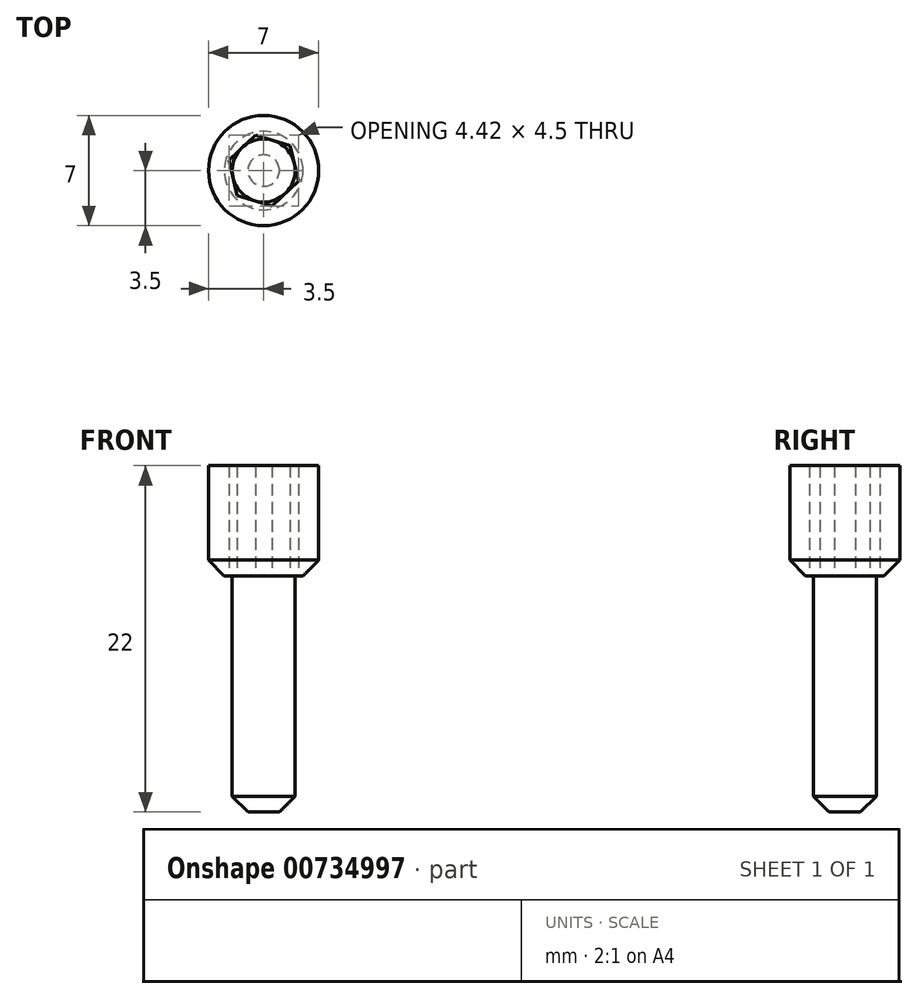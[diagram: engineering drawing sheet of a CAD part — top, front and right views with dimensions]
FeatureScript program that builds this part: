
annotation { "Feature Type Name" : "Feature", "Feature Type Description" : "" }
export const myFeature = defineFeature(function(context is Context, id is Id, definition is map)
    precondition{}
    {
        {
            var Q0;
            Q0=qCreatedBy(makeId("Top.planeOp"),FACE);
            var sketch = newSketch(context, id + "F0", { "sketchPlane" : qUnion([Q0])});
            skCircle(sketch, "E0", {"center": v(0, 0) * mm, "radius": 3.5 * mm});
            skCircle(sketch, "E1.cCircle", {"center": v(0, 0) * mm, "radius": 2 * mm, "construction": true});
            skLineSegment(sketch, "E1.0", {"start": v(2.21, -0.67) * mm, "end": v(0.53, -2.25) * mm});
            skLineSegment(sketch, "E1.1", {"start": v(0.53, -2.25) * mm, "end": v(-1.68, -1.58) * mm});
            skLineSegment(sketch, "E1.2", {"start": v(-1.68, -1.58) * mm, "end": v(-2.21, 0.67) * mm});
            skLineSegment(sketch, "E1.3", {"start": v(-2.21, 0.67) * mm, "end": v(-0.53, 2.25) * mm});
            skLineSegment(sketch, "E1.4", {"start": v(-0.53, 2.25) * mm, "end": v(1.68, 1.58) * mm});
            skLineSegment(sketch, "E1.5", {"start": v(1.68, 1.58) * mm, "end": v(2.21, -0.67) * mm});
            skPoint(sketch, "E1.0.midPoint", {"position": v(1.37, -1.46) * mm});
            skSolve(sketch);
        }
        {
            var Q0;
            Q0=makeQuery(id+"F0.imprint","IMPRINT",FACE,{"disambiguationData":[TD([[makeQuery(id+"F0.imprint","IMPRINT",EDGE,{"derivedFrom":sQuery(id+"F0.wireOp",EDGE,"E0")}),1.0]])]});
            extrude(context, id + "F1", {"entities" : qUnion([Q0]), "depth" : 7 * mm, "offsetDistance" : 25 * mm});
        }
        {
            var Q0;
            Q0=qCreatedBy(makeId("Top.planeOp"),FACE);
            var sketch = newSketch(context, id + "F2", { "sketchPlane" : qUnion([Q0])});
            skCircle(sketch, "E2.cCircle", {"center": v(0, 0) * mm, "radius": 2 * mm, "construction": true});
            skLineSegment(sketch, "E2.0", {"start": v(1.68, 1.58) * mm, "end": v(2.21, -0.67) * mm});
            skLineSegment(sketch, "E2.1", {"start": v(2.21, -0.67) * mm, "end": v(0.53, -2.25) * mm});
            skLineSegment(sketch, "E2.2", {"start": v(0.53, -2.25) * mm, "end": v(-1.68, -1.58) * mm});
            skLineSegment(sketch, "E2.3", {"start": v(-1.68, -1.58) * mm, "end": v(-2.21, 0.67) * mm});
            skLineSegment(sketch, "E2.4", {"start": v(-2.21, 0.67) * mm, "end": v(-0.53, 2.25) * mm});
            skLineSegment(sketch, "E2.5", {"start": v(-0.53, 2.25) * mm, "end": v(1.68, 1.58) * mm});
            skPoint(sketch, "E2.0.midPoint", {"position": v(1.95, 0.46) * mm});
            skCircle(sketch, "E3", {"center": v(0, 0) * mm, "radius": 2 * mm});
            skSolve(sketch);
        }
        {
            var Q0;
            Q0=makeQuery(id+"F2.imprint","IMPRINT",FACE,{"disambiguationData":[TD([[makeQuery(id+"F2.imprint","IMPRINT",EDGE,{"derivedFrom":sQuery(id+"F2.wireOp",EDGE,"E3")}),1.0]])]});
            extrude(context, id + "F3", {"entities" : qUnion([Q0]), "depth" : -15 * mm, "offsetDistance" : 25 * mm});
        }
        {
            var Q0;
            Q0=makeQuery(id+"F3.opExtrude","CAP_EDGE",EDGE,{"disambiguationData":[OSD([sQuery(id+"F2.wireOp",EDGE,"E3")])],"isStart":false});
            var Q1;
            Q1=makeQuery(id+"F1.opExtrude","CAP_EDGE",EDGE,{"disambiguationData":[OSD([sQuery(id+"F0.wireOp",EDGE,"E0")])],"isStart":true});
            chamfer(context, id + "F4", {"entities" : qUnion([Q0, Q1]), "width" : 1 * mm, "tangentPropagation" : true});
        }
    });
